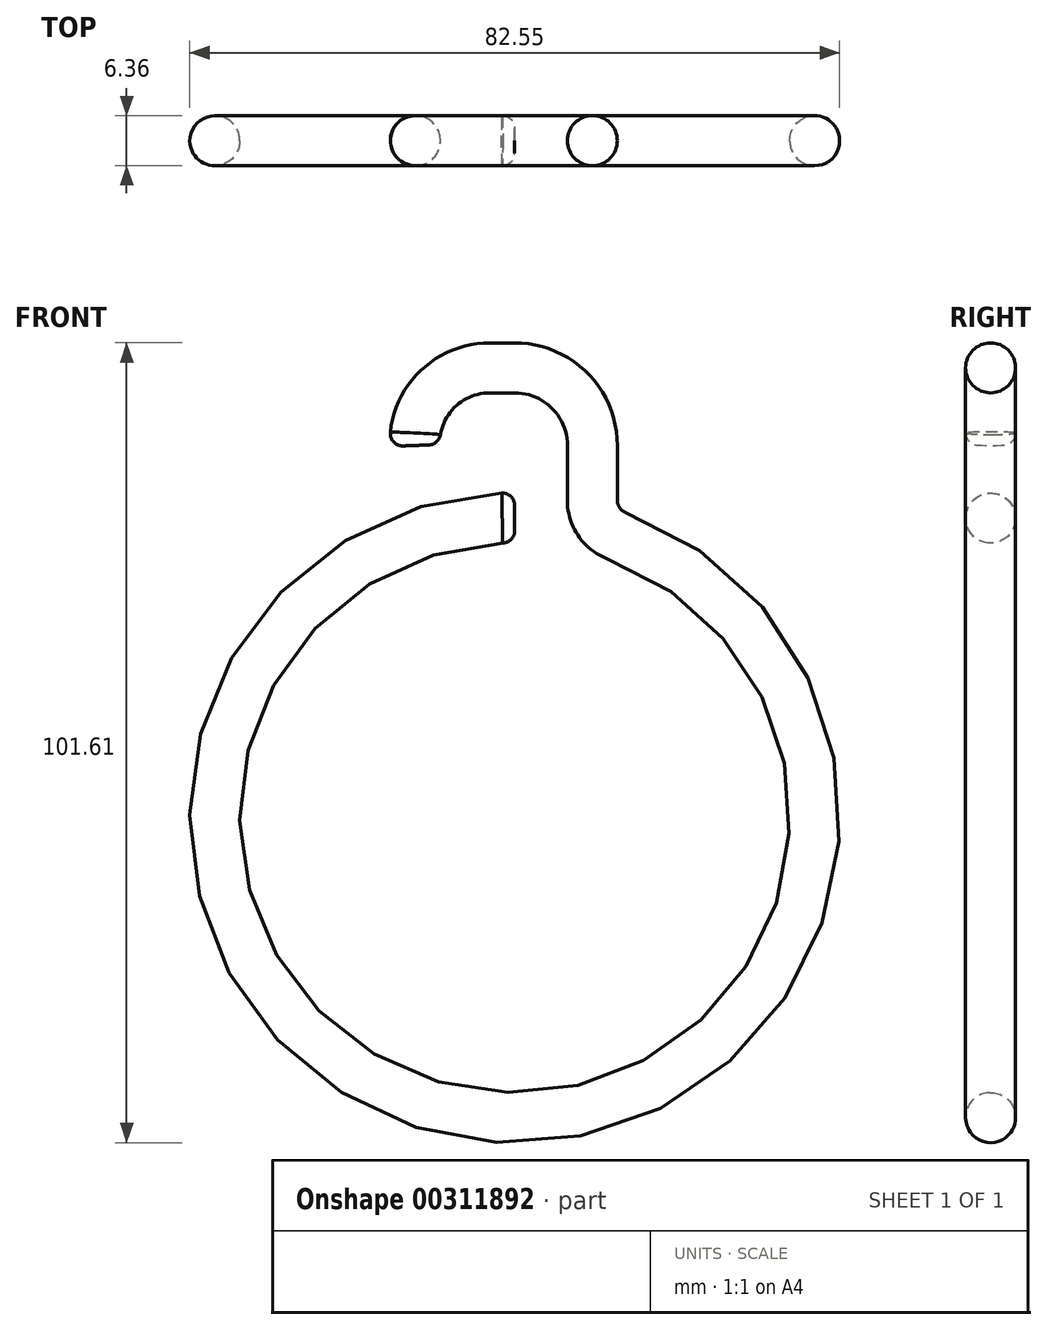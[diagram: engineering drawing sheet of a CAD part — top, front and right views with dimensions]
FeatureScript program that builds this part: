
annotation { "Feature Type Name" : "Feature", "Feature Type Description" : "" }
export const myFeature = defineFeature(function(context is Context, id is Id, definition is map)
    precondition{}
    {
        {
            var Q0;
            Q0=qCreatedBy(makeId("Front.planeOp"),FACE);
            var sketch = newSketch(context, id + "F0", { "sketchPlane" : qUnion([Q0])});
            skLineSegment(sketch, "E0", {"start": v(0, -9.86) * mm, "end": v(0, -16.86) * mm});
            skArc(sketch, "E1", {"start": v(-9.86, -19.05) * mm, "mid": v(-16.46, -94.67) * mm, "end": v(3.14, -21.34) * mm});
            skLineSegment(sketch, "E2", {"start": v(-9.86, -57.15) * mm, "end": v(0, -20.35) * mm, "construction": true});
            skLineSegment(sketch, "E3", {"start": v(-9.86, -57.15) * mm, "end": v(-9.86, -19.05) * mm, "construction": true});
            skArc(sketch, "E4", {"start": v(0, -9.86) * mm, "mid": v(-2.89, -2.89) * mm, "end": v(-9.86, 0) * mm});
            skPoint(sketch, "E5.orphan", {"position": v(0, 0) * mm});
            skArc(sketch, "E6", {"start": v(0, -16.86) * mm, "mid": v(0.86, -19.6) * mm, "end": v(3.14, -21.34) * mm});
            skLineSegment(sketch, "E7", {"start": v(-9.86, -57.15) * mm, "end": v(-9.86, 0) * mm, "construction": true});
            skLineSegment(sketch, "E8", {"start": v(-9.86, 0) * mm, "end": v(-13.04, 0) * mm});
            skArc(sketch, "E9", {"start": v(-13.04, 0) * mm, "mid": v(-19.89, -2.9) * mm, "end": v(-22.56, -9.86) * mm});
            skLineSegment(sketch, "E10", {"start": v(0, -9.86) * mm, "end": v(-34.72, -9.86) * mm, "construction": true});
            skSolve(sketch);
        }
        {
            var Q0;
            Q0=sQuery(id+"F0.wireOp",EDGE,"E3");
            cPlane(context, id + "F1", {"entities" : qUnion([Q0]), "cplaneType" : CPlaneType.LINE_ANGLE, "offset" : 25.4 * mm, "angle" : 0 * degree, "width" : 152.4 * mm, "height" : 152.4 * mm});
        }
        {
            var Q0;
            Q0=qCreatedBy(id+"F1.planeOp",FACE);
            var sketch = newSketch(context, id + "F2", { "sketchPlane" : qUnion([Q0])});
            skCircle(sketch, "E11", {"center": v(0, -19.05) * mm, "radius": 3.18 * mm});
            skSolve(sketch);
        }
        {
            var Q0;
            Q0=makeQuery(id+"F2.imprint","IMPRINT",FACE,{"disambiguationData":[TD([[makeQuery(id+"F2.imprint","IMPRINT",EDGE,{"derivedFrom":sQuery(id+"F2.wireOp",EDGE,"E11")}),1.0]])]});
            var Q1;
            Q1=sQuery(id+"F0.wireOp",EDGE,"E1");
            var Q2;
            Q2=sQuery(id+"F0.wireOp",EDGE,"E6");
            var Q3;
            Q3=sQuery(id+"F0.wireOp",EDGE,"E0");
            var Q4;
            Q4=sQuery(id+"F0.wireOp",EDGE,"E4");
            var Q5;
            Q5=sQuery(id+"F0.wireOp",EDGE,"P7seRi9g-FBT0-5J7L-LNWv-KyRFAVixfbLV");
            var Q6;
            Q6=sQuery(id+"F0.wireOp",EDGE,"E8");
            var Q7;
            Q7=sQuery(id+"F0.wireOp",EDGE,"E9");
            sweep(context, id + "F3", {"profiles" : qUnion([Q0]), "path" : qUnion([Q1, Q2, Q3, Q4, Q5, Q6, Q7])});
        }
        {
            var Q0;
            Q0=makeQuery(id+"F3.opSweep","CAP_EDGE",EDGE,{"disambiguationData":[OSD([sQuery(id+"F0.wireOp",VERTEX,"E1.start"),sQuery(id+"F2.wireOp",EDGE,"E11")])],"isStart":true});
            var Q1;
            Q1=makeQuery(id+"F3.opSweep","CAP_EDGE",EDGE,{"disambiguationData":[OSD([sQuery(id+"F0.wireOp",VERTEX,"P7seRi9g-FBT0-5J7L-LNWv-KyRFAVixfbLV.end"),sQuery(id+"F2.wireOp",EDGE,"E11")])],"isStart":false});
            fillet(context, id + "F4", {"entities" : qUnion([Q0, Q1]), "radius" : 1.59 * mm, "tangentPropagation" : true, "allowEdgeOverflow" : false});
        }
    });
